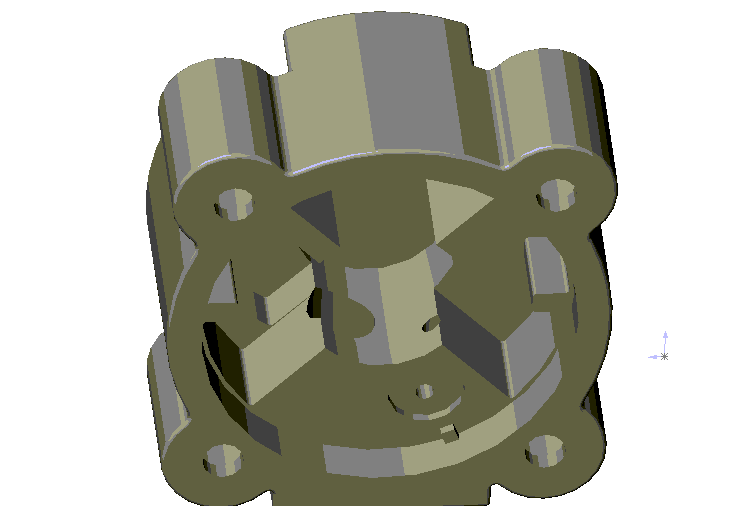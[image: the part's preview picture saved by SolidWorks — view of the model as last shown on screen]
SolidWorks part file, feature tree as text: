
SOLIDWORKS PART (.sldprt)
format: sldprt  version: not decoded by parser v0  size: 1,074,176 bytes
history: native  units: mm
features: fillet x24, sketch x22, cut_extrude x11, hole x4, plane x3, extrude x3 + 1 further entry (+6 scaffold rows collapsed)
feature tree (74):
  scaffold x6  (default folders/planes/origin — collapsed)
  "Corps de surface"
  plane  "Plan1"
  plane  "Plan2"
  plane  "Plan3"
  sketch  "Esquisse1"
  extrude  "Base-Extrusion"  Depth=50mm
  sketch  "Esquisse2"  dims[D1=45.0mm D4=16.0mm D5=16.0mm D6=16.0mm D7=16.0mm D2=50.0mm D3=50.0mm D8=15.0mm D9=15.0mm D10=15.0mm D11=15.0mm D12=15.0mm D13=15.0mm D14=15.0mm D15=15.0mm]
  cut_extrude  "Enlèv. mat.-Extru.5"  Depth=46mm
  sketch  "Esquisse7"  dims[c1.D3=40.0mm c1.D4=40.0mm c1.D5=33.0mm c1.D1=35.0mm c1.D2=35.0mm c2.D3=50.0mm c2.D1=50.0mm c2.D2=50.0mm c3.D3=35.0mm c3.D4=35.0mm]
  cut_extrude  "Enlèv. mat.-Extru.9"  Depth=15mm
  sketch  "Esquisse11"  dims[D1=36.0mm D2=50.0mm D3=50.0mm]
  cut_extrude  "Enlèv. mat.-Extru.12"  Depth=44mm
  sketch  "Esquisse12"  dims[D1=27.0mm D2=27.0mm D3=27.0mm D4=27.0mm D5=97.0mm D6=1.0mm]
  cut_extrude  "Enlèv. mat.-Extru.13"  [1 undecoded]
  sketch  "Esquisse13"  dims[D1=9.0mm]
  cut_extrude  "Enlèv. mat.-Extru.14"  [1 undecoded]
  fillet  "Congé1"  Radius=2mm
  fillet  "Congé2"  Radius=2mm
  fillet  "Congé5"  Radius=2mm
  fillet  "Congé6"  Radius=2mm
  fillet  "Congé7"  Radius=2mm
  fillet  "Congé8"  Radius=2mm
  sketch  "Esquisse14"  dims[D1=45.0mm]
  extrude  "Boss.-Extru.1"  Depth=5mm
  fillet  "Congé9"  Radius=1mm
  fillet  "Congé10"  Radius=2mm
  fillet  "Congé11"  Radius=2mm
  fillet  "Congé12"  Radius=2mm
  fillet  "Congé15"  Radius=2mm
  fillet  "Congé16"  Radius=2mm
  fillet  "Congé17"  Radius=2mm
  fillet  "Congé18"  Radius=1mm
  fillet  "Congé19"  Radius=0.5mm
  fillet  "Congé20"  Radius=0.5mm
  fillet  "Congé21"  Radius=0.5mm
  fillet  "Congé22"  Radius=0.5mm
  sketch  "Esquisse15"  dims[c1.D1=92.0mm c1.D2=51.0mm c1.D3=44.0mm c1.D4=5.0mm c1.D5=5.0mm c2.D4=~25.495098mm]
  cut_extrude  "Enlèv. mat.-Extru.15"  Depth=2mm
  sketch  "Esquisse16"  dims[D1=34.0mm]
  cut_extrude  "Enlèv. mat.-Extru.16"  Depth=2mm
  fillet  "Congé23"  Radius=1mm
  fillet  "Congé25"  Radius=0.5mm
  fillet  "Congé26"  Radius=0.5mm
  fillet  "Congé27"  Radius=0.5mm
  fillet  "Congé28"  Radius=0.5mm
  fillet  "Congé32"  Radius=1mm
  sketch  "Esquisse17"  dims[c1.D3=5.0mm c1.D7=43.0mm c1.D1=15.0mm c1.D2=7.5mm c2.D3=7.5mm c2.D4=7.5mm c2.D5=7.5mm c2.D6=7.5mm]
  extrude  "Boss.-Extru.2"  Depth=1mm
  sketch  "Esquisse18"  dims[c1.D1=82.0mm c1.D2=15.0mm c1.D3=~12.454202mm c2.D3=~4.980751deg c3.D3=3.0mm c3.D4=3.0mm]
  sketch  "Esquisse19"  dims[D1=82.0mm]
  cut_extrude  "Enlèv. mat.-Extru.18"  Depth=8mm
  cut_extrude  "Enlèv. mat.-Extru.19"  Depth=10mm
  sketch  "Esquisse20"  dims[c1.D1=80.0mm c1.D8=1.0mm c1.D9=0.5mm c1.D10=1.0mm c1.D2=2.0mm c1.D3=4.0mm c1.D4=3.0mm c1.D5=5.0mm c1.D6=32.0mm c1.D7=23.0mm c2.D8=~9.369165mm c3.D8=45.0deg]
  cut_extrude  "Enlèv. mat.-Extru.20"  Depth=20mm
  sketch  "Esquisse21"  dims[D1=1.0mm D2=1.0mm D3=36.0mm D4=36.0mm D5=36.0mm D6=1.0mm D7=40.0mm D8=40.0mm]
  cut_extrude  "Enlèv. mat.-Extru.22"  Depth=10mm
  hole  "Perçage1"  Diameter=15mm Depth=33.714005mm
  sketch  "Esquisse24"  dims[D1=26.0mm D2=16.0mm]
  sketch  "Esquisse23"  dims[Diamètre=15.0mm Profondeur=~33.714005mm]
  hole  "Perçage2"  Diameter=4mm Depth=36.016485mm
  sketch  "Esquisse26"  dims[D1=19.0mm D2=35.0mm]
  sketch  "Esquisse25"  dims[Diamètre=4.0mm Profondeur=~36.016485mm]
  hole  "Perçage3"  Diameter=17mm Depth=2mm
  sketch  "Esquisse28"  dims[D1=~25.600723mm D2=24.0mm D3=13.0mm]
  sketch  "Esquisse27"  dims[Diamètre=17.0mm Profondeur=2.0mm]
  hole  "Perçage4"  Diameter=4mm Depth=15mm
  sketch  "Esquisse30"  dims[D1=13.0mm D2=22.0mm]
  sketch  "Esquisse29"  dims[Diamètre=4.0mm Profondeur=15.0mm]
decode coverage: 61 of 64 modeling features carry decoded parameters; 1 rows unclassified (native names shown)
note: ~ marks probable driven/reference dimensions
note: 2 parameter values undecoded
summary: Diameter pulled from absorbed wizard sketch
note: suppression state not decoded; provenance and decode notes live in map.json
